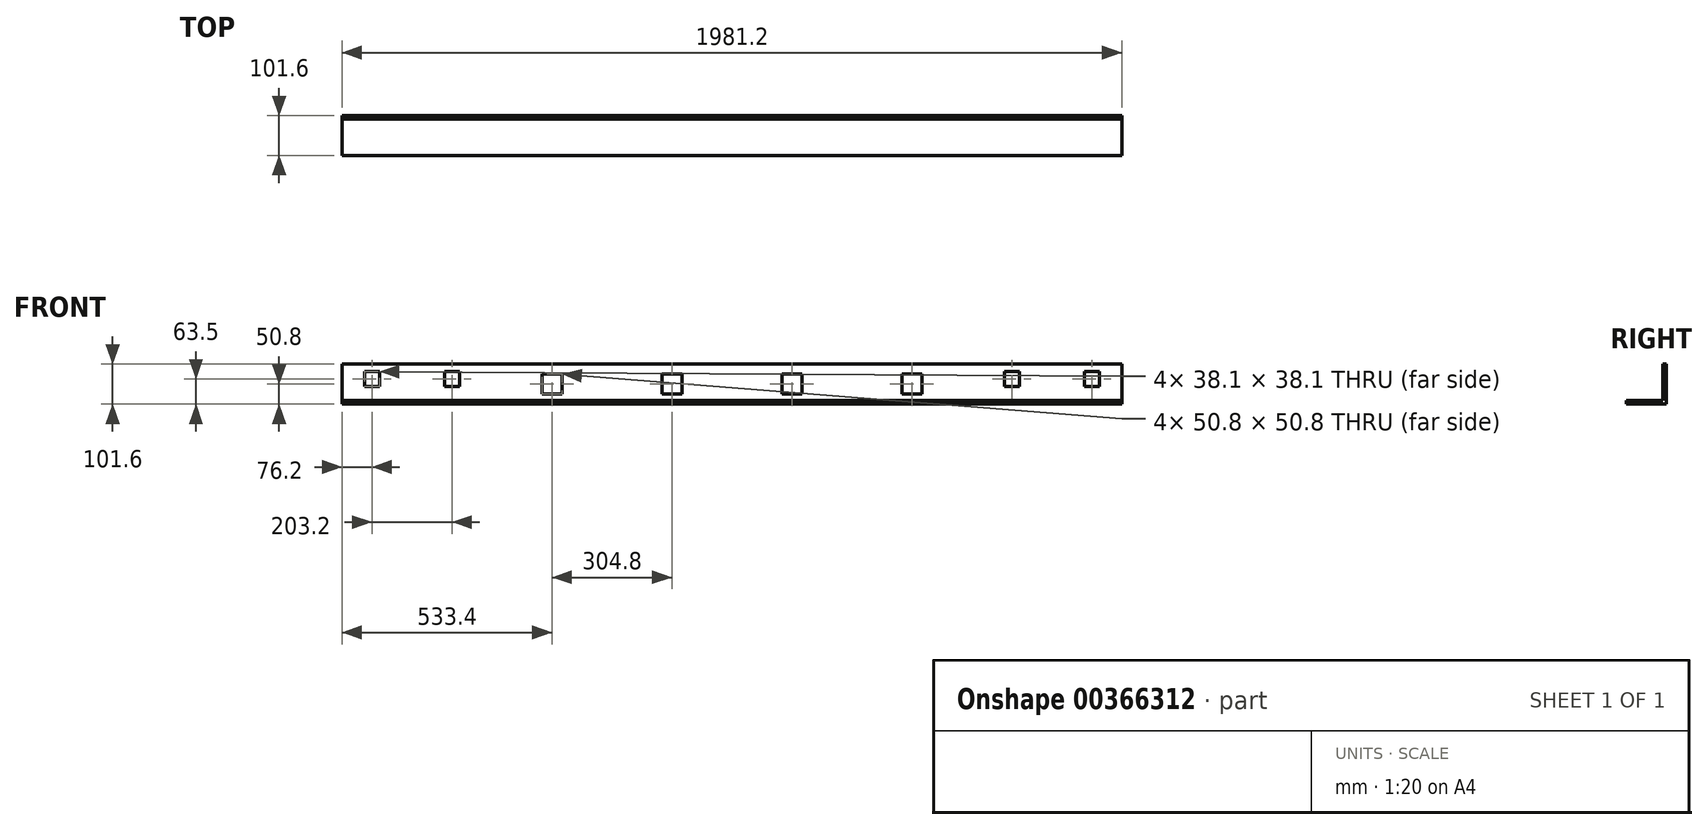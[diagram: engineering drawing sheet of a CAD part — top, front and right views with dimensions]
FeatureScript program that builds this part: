
annotation { "Feature Type Name" : "Feature", "Feature Type Description" : "" }
export const myFeature = defineFeature(function(context is Context, id is Id, definition is map)
    precondition{}
    {
        {
            var Q0;
            Q0=qCreatedBy(makeId("Front.planeOp"),FACE);
            var sketch = newSketch(context, id + "F0", { "sketchPlane" : qUnion([Q0])});
            skLineSegment(sketch, "E0.bottom", {"start": v(0, 0) * mm, "end": v(1981.2, 0) * mm});
            skLineSegment(sketch, "E0.top", {"start": v(0, 101.6) * mm, "end": v(1981.2, 101.6) * mm});
            skLineSegment(sketch, "E0.left", {"start": v(0, 0) * mm, "end": v(0, 101.6) * mm});
            skLineSegment(sketch, "E0.right", {"start": v(1981.2, 0) * mm, "end": v(1981.2, 101.6) * mm});
            skLineSegment(sketch, "E1.bottom", {"start": v(57.15, 44.45) * mm, "end": v(95.25, 44.45) * mm});
            skLineSegment(sketch, "E1.top", {"start": v(57.15, 82.55) * mm, "end": v(95.25, 82.55) * mm});
            skLineSegment(sketch, "E1.left", {"start": v(57.15, 44.45) * mm, "end": v(57.15, 82.55) * mm});
            skLineSegment(sketch, "E1.right", {"start": v(95.25, 44.45) * mm, "end": v(95.25, 82.55) * mm});
            skLineSegment(sketch, "E2.bottom", {"start": v(260.35, 44.45) * mm, "end": v(298.45, 44.45) * mm});
            skLineSegment(sketch, "E2.top", {"start": v(260.35, 82.55) * mm, "end": v(298.45, 82.55) * mm});
            skLineSegment(sketch, "E2.left", {"start": v(260.35, 44.45) * mm, "end": v(260.35, 82.55) * mm});
            skLineSegment(sketch, "E2.right", {"start": v(298.45, 44.45) * mm, "end": v(298.45, 82.55) * mm});
            skPoint(sketch, "E3", {"position": v(76.2, 44.45) * mm});
            skPoint(sketch, "E4", {"position": v(279.4, 44.45) * mm});
            skLineSegment(sketch, "E5.bottom", {"start": v(508, 25.4) * mm, "end": v(558.8, 25.4) * mm});
            skLineSegment(sketch, "E5.top", {"start": v(508, 76.2) * mm, "end": v(558.8, 76.2) * mm});
            skLineSegment(sketch, "E5.left", {"start": v(508, 25.4) * mm, "end": v(508, 76.2) * mm});
            skLineSegment(sketch, "E5.right", {"start": v(558.8, 25.4) * mm, "end": v(558.8, 76.2) * mm});
            skLineSegment(sketch, "E6.bottom", {"start": v(812.8, 25.4) * mm, "end": v(863.6, 25.4) * mm});
            skLineSegment(sketch, "E6.top", {"start": v(812.8, 76.2) * mm, "end": v(863.6, 76.2) * mm});
            skLineSegment(sketch, "E6.left", {"start": v(812.8, 25.4) * mm, "end": v(812.8, 76.2) * mm});
            skLineSegment(sketch, "E6.right", {"start": v(863.6, 25.4) * mm, "end": v(863.6, 76.2) * mm});
            skLineSegment(sketch, "E7.bottom", {"start": v(1117.6, 25.4) * mm, "end": v(1168.4, 25.4) * mm});
            skLineSegment(sketch, "E7.top", {"start": v(1117.6, 76.2) * mm, "end": v(1168.4, 76.2) * mm});
            skLineSegment(sketch, "E7.left", {"start": v(1117.6, 25.4) * mm, "end": v(1117.6, 76.2) * mm});
            skLineSegment(sketch, "E7.right", {"start": v(1168.4, 25.4) * mm, "end": v(1168.4, 76.2) * mm});
            skPoint(sketch, "E8", {"position": v(533.4, 25.4) * mm});
            skPoint(sketch, "E9", {"position": v(838.2, 25.4) * mm});
            skPoint(sketch, "E10", {"position": v(1143, 25.4) * mm});
            skLineSegment(sketch, "E11.bottom", {"start": v(1422.4, 25.4) * mm, "end": v(1473.2, 25.4) * mm});
            skLineSegment(sketch, "E11.top", {"start": v(1422.4, 76.2) * mm, "end": v(1473.2, 76.2) * mm});
            skLineSegment(sketch, "E11.left", {"start": v(1422.4, 25.4) * mm, "end": v(1422.4, 76.2) * mm});
            skLineSegment(sketch, "E11.right", {"start": v(1473.2, 25.4) * mm, "end": v(1473.2, 76.2) * mm});
            skPoint(sketch, "E12", {"position": v(1447.8, 25.4) * mm});
            skLineSegment(sketch, "E13.bottom", {"start": v(1682.75, 44.45) * mm, "end": v(1720.85, 44.45) * mm});
            skLineSegment(sketch, "E13.top", {"start": v(1682.75, 82.55) * mm, "end": v(1720.85, 82.55) * mm});
            skLineSegment(sketch, "E13.left", {"start": v(1682.75, 44.45) * mm, "end": v(1682.75, 82.55) * mm});
            skLineSegment(sketch, "E13.right", {"start": v(1720.85, 44.45) * mm, "end": v(1720.85, 82.55) * mm});
            skLineSegment(sketch, "E14.bottom", {"start": v(1885.95, 44.45) * mm, "end": v(1924.05, 44.45) * mm});
            skLineSegment(sketch, "E14.top", {"start": v(1885.95, 82.55) * mm, "end": v(1924.05, 82.55) * mm});
            skLineSegment(sketch, "E14.left", {"start": v(1885.95, 44.45) * mm, "end": v(1885.95, 82.55) * mm});
            skLineSegment(sketch, "E14.right", {"start": v(1924.05, 44.45) * mm, "end": v(1924.05, 82.55) * mm});
            skPoint(sketch, "E15", {"position": v(1701.8, 44.45) * mm});
            skPoint(sketch, "E16", {"position": v(1905, 44.45) * mm});
            skSolve(sketch);
        }
        {
            var Q0;
            Q0=makeQuery(id+"F0.imprint","IMPRINT",FACE,{"disambiguationData":[TD([[makeQuery(id+"F0.imprint","IMPRINT",EDGE,{"derivedFrom":sQuery(id+"F0.wireOp",EDGE,"E0.bottom")}),1.0]])]});
            extrude(context, id + "F1", {"entities" : qUnion([Q0]), "depth" : 9.52 * mm});
        }
        {
            var Q0;
            Q0=makeQuery(id+"F1.opExtrude","CAP_FACE",FACE,{"disambiguationData":[OSD([sQuery(id+"F0.wireOp",EDGE,"E0.bottom"),sQuery(id+"F0.wireOp",EDGE,"E0.top"),sQuery(id+"F0.wireOp",EDGE,"E0.left"),sQuery(id+"F0.wireOp",EDGE,"E0.right"),sQuery(id+"F0.wireOp",EDGE,"E1.bottom"),sQuery(id+"F0.wireOp",EDGE,"E1.top"),sQuery(id+"F0.wireOp",EDGE,"E1.left"),sQuery(id+"F0.wireOp",EDGE,"E1.right"),sQuery(id+"F0.wireOp",EDGE,"E2.bottom"),sQuery(id+"F0.wireOp",EDGE,"E2.top"),sQuery(id+"F0.wireOp",EDGE,"E2.left"),sQuery(id+"F0.wireOp",EDGE,"E2.right"),sQuery(id+"F0.wireOp",EDGE,"E5.bottom"),sQuery(id+"F0.wireOp",EDGE,"E5.top"),sQuery(id+"F0.wireOp",EDGE,"E5.left"),sQuery(id+"F0.wireOp",EDGE,"E5.right"),sQuery(id+"F0.wireOp",EDGE,"E6.bottom"),sQuery(id+"F0.wireOp",EDGE,"E6.top"),sQuery(id+"F0.wireOp",EDGE,"E6.left"),sQuery(id+"F0.wireOp",EDGE,"E6.right"),sQuery(id+"F0.wireOp",EDGE,"E7.bottom"),sQuery(id+"F0.wireOp",EDGE,"E7.top"),sQuery(id+"F0.wireOp",EDGE,"E7.left"),sQuery(id+"F0.wireOp",EDGE,"E7.right"),sQuery(id+"F0.wireOp",EDGE,"E11.bottom"),sQuery(id+"F0.wireOp",EDGE,"E11.top"),sQuery(id+"F0.wireOp",EDGE,"E11.left"),sQuery(id+"F0.wireOp",EDGE,"E11.right"),sQuery(id+"F0.wireOp",EDGE,"E13.bottom"),sQuery(id+"F0.wireOp",EDGE,"E13.top"),sQuery(id+"F0.wireOp",EDGE,"E13.left"),sQuery(id+"F0.wireOp",EDGE,"E13.right"),sQuery(id+"F0.wireOp",EDGE,"E14.bottom"),sQuery(id+"F0.wireOp",EDGE,"E14.top"),sQuery(id+"F0.wireOp",EDGE,"E14.left"),sQuery(id+"F0.wireOp",EDGE,"E14.right")])],"isStart":false});
            var sketch = newSketch(context, id + "F2", { "sketchPlane" : qUnion([Q0])});
            skLineSegment(sketch, "E17.bottom", {"start": v(0, 0) * mm, "end": v(1981.2, 0) * mm});
            skLineSegment(sketch, "E17.top", {"start": v(0, 9.53) * mm, "end": v(1981.2, 9.53) * mm});
            skLineSegment(sketch, "E17.left", {"start": v(0, 0) * mm, "end": v(0, 9.53) * mm});
            skLineSegment(sketch, "E17.right", {"start": v(1981.2, 0) * mm, "end": v(1981.2, 9.53) * mm});
            skSolve(sketch);
        }
        {
            var Q0;
            Q0=makeQuery(id+"F2.imprint","IMPRINT",FACE,{"disambiguationData":[TD([[makeQuery(id+"F2.imprint","IMPRINT",EDGE,{"derivedFrom":sQuery(id+"F2.wireOp",EDGE,"E17.bottom")}),1.0]])]});
            extrude(context, id + "F3", {"entities" : qUnion([Q0]), "operationType" : NewBodyOperationType.ADD, "depth" : 92.07 * mm});
        }
    });
